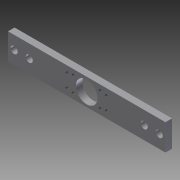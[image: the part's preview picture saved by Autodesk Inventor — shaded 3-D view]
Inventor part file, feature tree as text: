
AUTODESK INVENTOR PART (.ipt)
format: ipt  version: 2011 (Build 150239000, 239)  size: 126,976 bytes
history: native  units: in
note: dims shown in document units (in); Inventor stores cm internally (conversion verified against a paired STEP export)
features: sketch x7, hole x3, extrude x2, plane x2, mirror x2
ambient origin geometry x8: Origin, YZ Plane, XZ Plane, XY Plane, X Axis, Y Axis, Z Axis, Center Point
bodies: Solid1 (feature_tree)
feature tree (16):
  extrude  "Extrusion1"  Depth=0.374in
  extrude  "Extrusion2"  Depth=3.0in
  hole  "Hole1"  [1 undecoded]
  sketch  "Sketch5"  dims[d7=0.4134in d8=0.0625in d9=0.0in]
  plane  "Work Plane1"
  mirror  "Mirror1"
  hole  "Hole2"  [1 undecoded]
  sketch  "Sketch7"  dims[d15=120.0deg]
  plane  "Work Plane2"
  mirror  "Mirror2"
  hole  "Hole3"  [1 undecoded]
  sketch  "Sketch1"  dims[d0=0.51in d1=0.374in]
  sketch  "Sketch2"  dims[d2=0.75in d3=3.0in]
  sketch  "Sketch4"  dims[d4=0.5in d5=0.125in d6=0.0in]
  sketch  "Sketch6"  dims[d13=0.5906in d14=30.0deg]
  sketch  "Sketch8"  dims[d16=0.062in d17=0.75in d18=0.375in d19=0.25in d20=0.5635in d21=0.0315in d22=0.8108in d23=90.0deg d24=0.134in d25=0.75in d26=0.375in d27=0.25in d28=0.5635in d29=0.0315in d30=0.8108in d31=90.0deg d32=0.062in d33=0.75in d34=0.375in d35=0.25in d36=0.5635in d37=0.0315in d38=0.8108in d39=0.287in d40=0.1181in]
note: 3 required parameter values undecoded (feature->parameter linkage not recoverable at this tier; creation-order binding heuristic only, values carry confidence <= 0.55)
